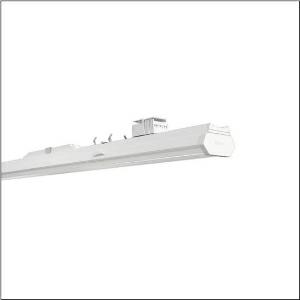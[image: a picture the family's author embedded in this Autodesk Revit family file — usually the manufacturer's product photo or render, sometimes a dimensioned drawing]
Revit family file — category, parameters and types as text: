
# Revit family: licross_11_protected_mo_51td12dn495g3s4
name_source: partatom
category: Lighting Fixtures
units: mm (PartAtom-declared; Revit-internal decimal feet)

## family parameters
Cut with Voids When Loaded = No
Host = Face
Light Source = No
Part Type = Normal
Room Calculation Point = No
Round Connector Dimension = Use Diameter
Shared = No

## types (1)
- --- (1 x LED, 980 lm, 6.8 W, 4000K)
    Apparent Load = 7 VA
    CIE Flux Codes = 73 92 98 99 100
    Color Rendering = 80
    Color Temperature = 4000K
    Default Elevation = 1800 mm
    Description = Licross 11 Protected MO, luminaire insert, of sheet steel, galvanised, coil coated, white, length: 1.500mm, width: 90mm, height: 101mm, LED rated luminous flux: 9.980lm, light colour: 840, SDCM (Standard Deviation of Colour Matching)MacAdam ≤ 2 SDCM (initial), control gear: DALI 2, with plug, 6-pole, with phase selection, for trunking rail, 9 or 11-core, mains connection: 220..240V, AC, 50/60Hz, rated input power: 61W, for trunking rail, 9-/11-core, internal wiring halogen-free, for emergency light function, converter,control gear: single battery element, battery: LiFePO4, 9Ah, primary light control with lens, of plastic, primary optical cover: cover, of PMMA, light emission: direct distribution, primary light characteristic: symmetric, protection rating (complete): IP54, insulation class (complete): insulation class I (protective earthing), certification: CE, UKCA, protection symbol: D if used in an environment with non-conductive dust loads with corresponding accessories, impact resistance: IK06, permissible ambient temperature for indoor applications: +5..+35°C, standard: EN 60598-2-22, LABS conformity tested according to VDMA 24364:2018-05, reducing of maximum allowable ambient temperature of 5°C with ceiling mounting, corresponds to IFS (International Featured Standards) requirements for safety and quality in the food industry, The light source and the operating device comply with the requirements of the Ecodesign Regulation (EU) 2019/2020 and are replaceable in accordance with this regulation, packaging unit: 1 piece
    Height = 92 mm
    Lamp = 1 x LED
    Lamp Light Flux = 980 lm
    Lamp Power = 6.8 W
    Lamp count = 1
    Length = 1500 mm
    Luminous efficacy = 144 lm/W
    Manufacturer = Siteco
    ModVariant = No
    Model = 51TD12DN495G3S4
    Mounting Place = Ceiling
    Mounting Type = Pendant
    Number of Poles = 1
    OnlyDefault = Yes
    Power Factor = 1
    Product Name = Licross 11 Protected MO
    Product group = luminaire insert | ceiling pendant
    ProductGroupID = 901
    Protection Class = Protection class I
    Protection Degree = IP 54
    RLX_Detail_Level = 1
    RLX_Emergency_Light_Flux = 0 lm
    RLX_Emergency_Type = 0
    RLX_Emergency_Type_DB = No
    RlxData = <blob elided: 25129 chars, md5=ec962ef4>
    Socket = socket
    Standby Power = 0 W
    System Light Flux = 980 lm
    System Power = 7 W
    Type Comments = : emergency light operation: 3 h
    Type Image = l_1256145.jpg
    URL = http://relux.com
    VarID = @adj_094437
    Voltage = 0 V
    Weight = 0.00 kg
    Width = 88 mm

## geometry (parser evidence)
native form markers: Blend x4, Sweep x9
no freeform markers — native parametric forms only
